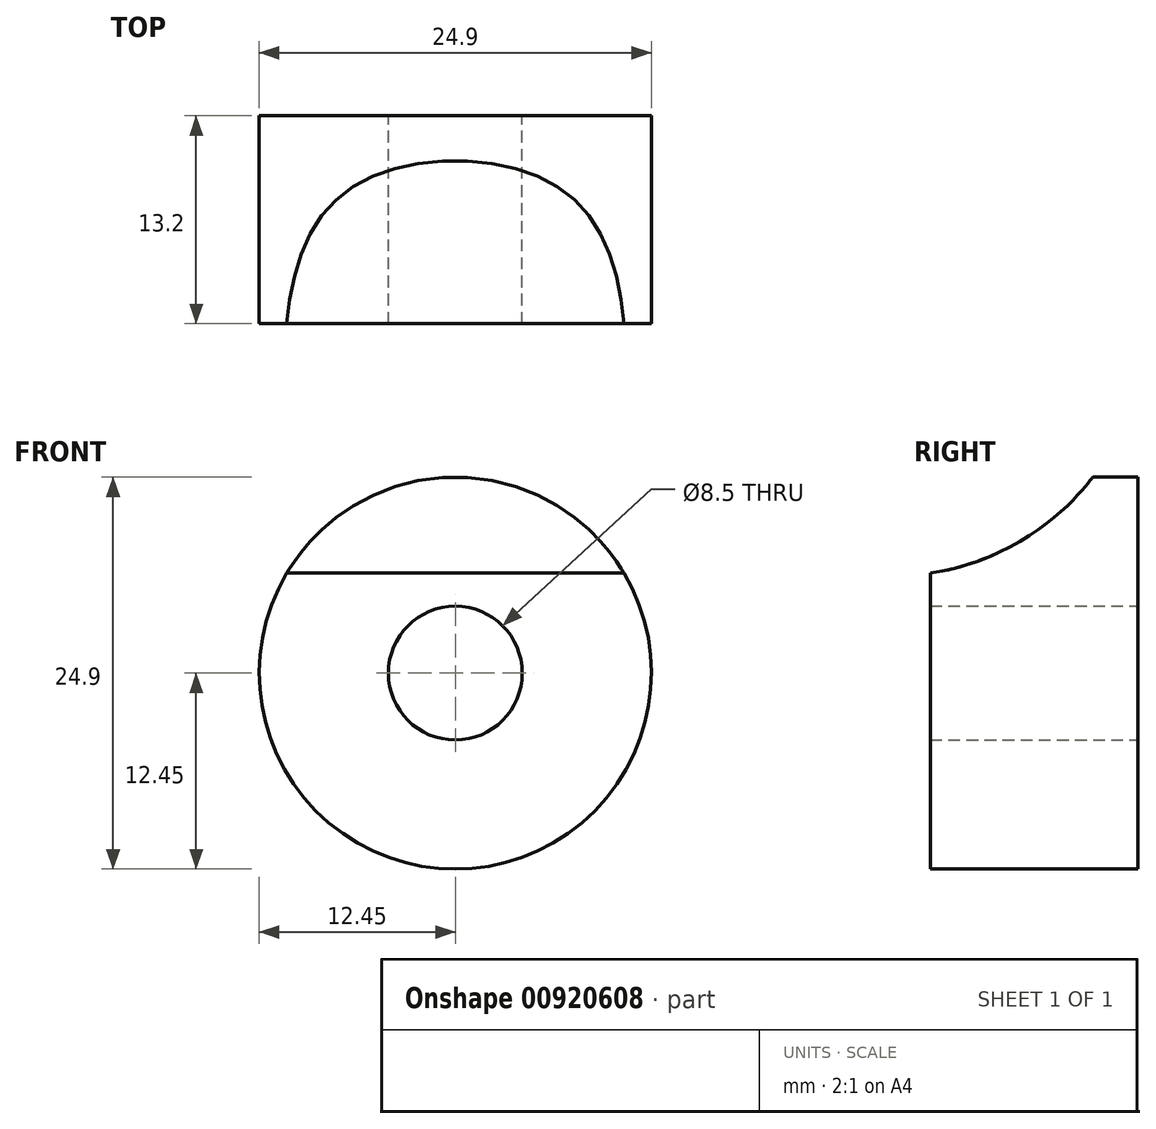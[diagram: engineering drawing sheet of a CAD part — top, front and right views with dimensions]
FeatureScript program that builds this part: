
annotation { "Feature Type Name" : "Feature", "Feature Type Description" : "" }
export const myFeature = defineFeature(function(context is Context, id is Id, definition is map)
    precondition{}
    {
        {
            var Q0;
            Q0=qCreatedBy(makeId("Front.planeOp"),FACE);
            var sketch = newSketch(context, id + "F0", { "sketchPlane" : qUnion([Q0])});
            skCircle(sketch, "E0", {"center": v(0, 0) * mm, "radius": 4.25 * mm});
            skCircle(sketch, "E1", {"center": v(0, 0) * mm, "radius": 12.45 * mm});
            skSolve(sketch);
        }
        {
            var Q0;
            Q0=makeQuery(id+"F0.imprint","IMPRINT",FACE,{"disambiguationData":[TD([[makeQuery(id+"F0.imprint","IMPRINT",EDGE,{"derivedFrom":sQuery(id+"F0.wireOp",EDGE,"E0")}),-1.0]])]});
            extrude(context, id + "F1", {"entities" : qUnion([Q0]), "depth" : 13.2 * mm, "offsetDistance" : 25 * mm});
        }
        {
            var Q0;
            Q0=qCreatedBy(makeId("Right.planeOp"),FACE);
            var sketch = newSketch(context, id + "F2", { "sketchPlane" : qUnion([Q0])});
            skLineSegment(sketch, "E2", {"start": v(-13.2, 12.45) * mm, "end": v(0, 12.45) * mm, "construction": true});
            skLineSegment(sketch, "E3", {"start": v(0, -12.45) * mm, "end": v(-13.2, -12.45) * mm, "construction": true});
            skLineSegment(sketch, "E4", {"start": v(-13.2, -12.45) * mm, "end": v(-13.2, 12.45) * mm, "construction": true});
            skLineSegment(sketch, "E5", {"start": v(-13.2, 12.45) * mm, "end": v(-13.2, 6.35) * mm});
            skLineSegment(sketch, "E6", {"start": v(-13.2, 12.45) * mm, "end": v(-2.87, 12.45) * mm});
            skArc(sketch, "E7", {"start": v(-13.2, 6.35) * mm, "mid": v(-7.44, 8.4) * mm, "end": v(-2.87, 12.45) * mm});
            skSolve(sketch);
        }
        {
            var Q0;
            Q0=makeQuery(id+"F2.imprint","IMPRINT",FACE,{"disambiguationData":[TD([[makeQuery(id+"F2.imprint","IMPRINT",EDGE,{"derivedFrom":sQuery(id+"F2.wireOp",EDGE,"E5")}),1.0]])]});
            extrude(context, id + "F3", {"entities" : qUnion([Q0]), "operationType" : NewBodyOperationType.REMOVE, "oppositeDirection" : true, "depth" : 25 * mm, "offsetDistance" : 25 * mm, "symmetric" : true});
        }
    });
